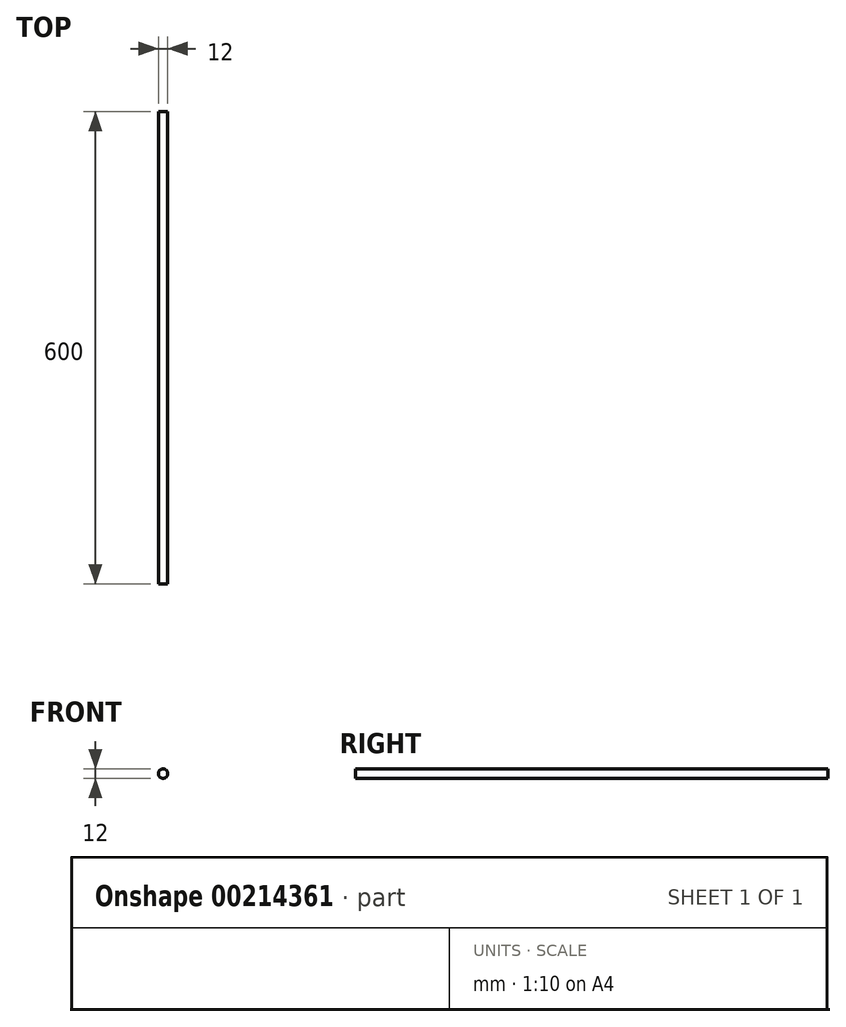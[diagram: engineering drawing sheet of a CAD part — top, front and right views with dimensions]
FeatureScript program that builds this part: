
annotation { "Feature Type Name" : "Feature", "Feature Type Description" : "" }
export const myFeature = defineFeature(function(context is Context, id is Id, definition is map)
    precondition{}
    {
        {
            var Q0;
            Q0=qCreatedBy(makeId("Front.planeOp"),FACE);
            var sketch = newSketch(context, id + "F0", { "sketchPlane" : qUnion([Q0])});
            skCircle(sketch, "E0", {"center": v(0, 0) * mm, "radius": 6 * mm});
            skSolve(sketch);
        }
        {
            var Q0;
            Q0=qSketchRegion(id+"F0",true);
            extrude(context, id + "F1", {"entities" : qUnion([Q0]), "depth" : 600 * mm});
        }
    });
